# Revit family: xFlush_Valve-Urinal-Wall_Box-American_Standard-Concealed-Back_Spud_Series
name_source: partatom
category: Plumbing Fixtures
revit_build: Autodesk Revit 2014 (Build: 20130308_1515(x64)
units: mm (PartAtom-declared; Revit-internal decimal feet)

## types (2) — shared parameters
ADA Compliant = Yes
Assembly Code = D2020300
CW Connection = Yes
CWFU = 5
Cold Water Connection Diameter = 3/4"
Cold Water Connection Radius = 3/8"
Cold Water Connection Width = 4 1/4"
Default Elevation = 0"
Description = Selectronic Sensor Operated Concealed Urinal Flush Valve
HW Connection = No
Installation Type = Concealed, Back Spud
Manufacturer = American Standard
Material = Metal-American Standard-002-Polished Chrome
PK00.BBU - Battery Back-Up = Yes
PK00.CRP-P2 Lithium Battery - Power Kit = No
PK00.HAC - Hard Wired AC - Power Kit = No
PK00.MAC - Multi-AC - Power Kit = No
PK00.PAC - Plug-In AC- Power Kit = No
PK00.WRK - PWRX 10-Year Battery - Power Kit = No
Price = Prices may vary. Please consult Manufacturer Representative for most up-to-date price list.
Product Documentation Link = https://www.americanstandard-us.com
Product Page URL = https://www.americanstandard-us.com
Tube Length = 11 3/8"
Type Comments = Power Kits Must Be Purchased Separately.
URL = http://www.americanstandard-us.com
Valve Distance From Finished Wall = 5"
Vent Connection = No
Warranty Information = 1 Year Limited Warranty
Waste Connection = No
zero-valued in all types: HWFU, WFU

## per-type parameters (varying)
| type | Flush Rate |
| 606B.505 | 0.5 gpf/1.9 Lpf |
| 606B.501 | 0.125 gpf/0.5 Lpf |

note: column(s) folded — value = type name in every type: Model

## geometry (parser evidence)
native form markers: Sweep x2
no freeform markers — native parametric forms only
